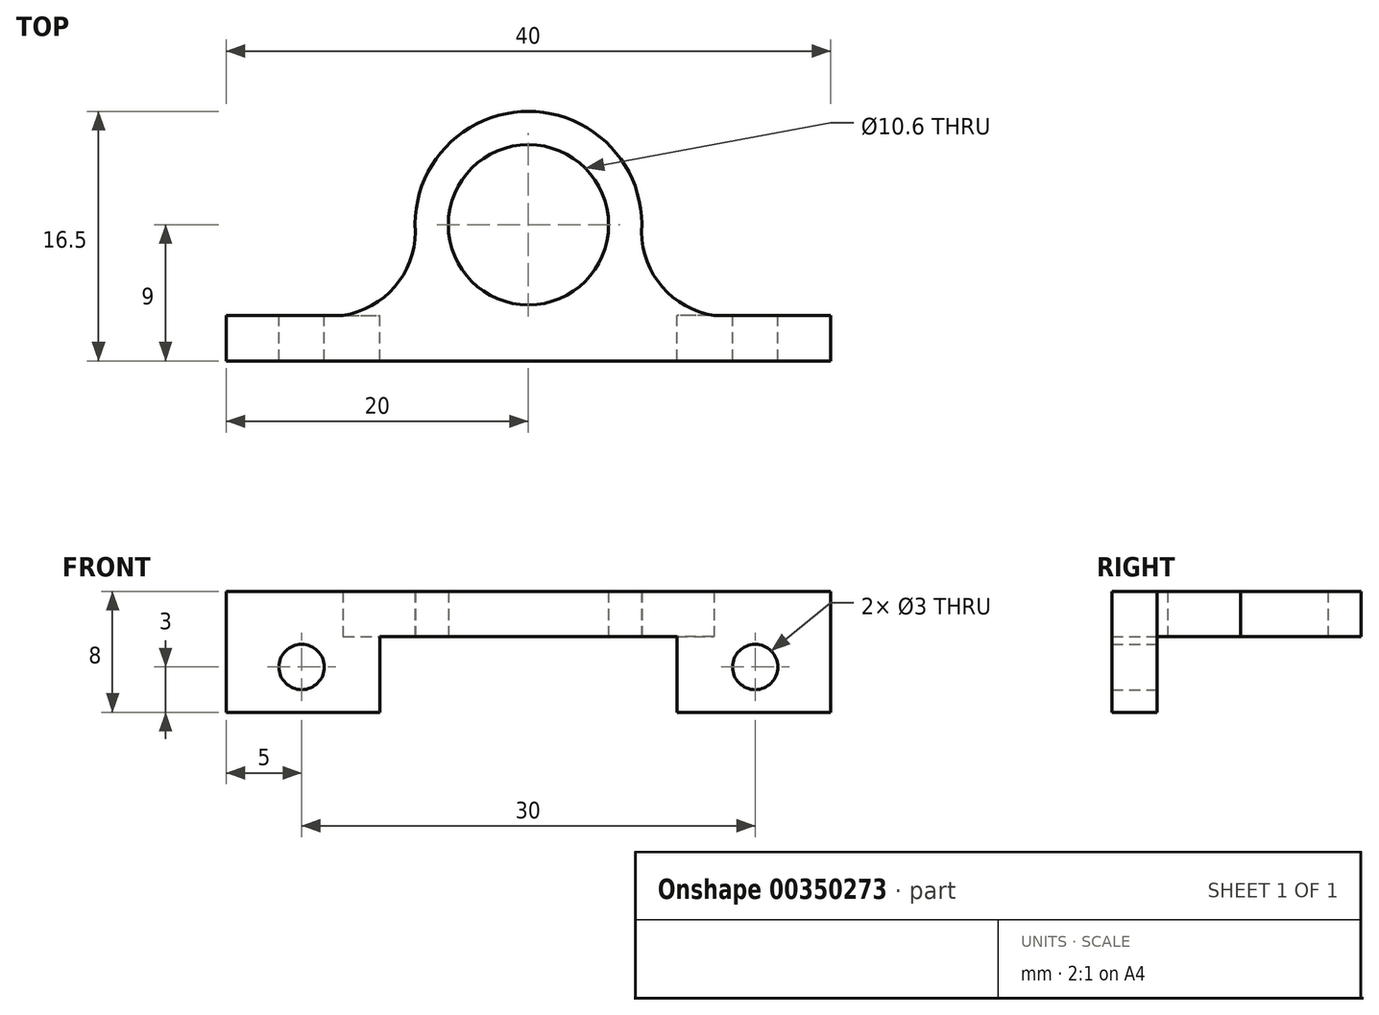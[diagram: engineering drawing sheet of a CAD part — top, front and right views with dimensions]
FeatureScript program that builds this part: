
annotation { "Feature Type Name" : "Feature", "Feature Type Description" : "" }
export const myFeature = defineFeature(function(context is Context, id is Id, definition is map)
    precondition{}
    {
        {
            var Q0;
            Q0=qCreatedBy(makeId("Top.planeOp"),FACE);
            var sketch = newSketch(context, id + "F0", { "sketchPlane" : qUnion([Q0])});
            skLineSegment(sketch, "E0.bottom", {"start": v(-20, 0) * mm, "end": v(-12.26, 0) * mm});
            skLineSegment(sketch, "E0.top", {"start": v(-20, -3) * mm, "end": v(0, -3) * mm});
            skLineSegment(sketch, "E0.left", {"start": v(-20, 0) * mm, "end": v(-20, -3) * mm});
            skCircle(sketch, "E1", {"center": v(0, 6) * mm, "radius": 5.3 * mm});
            skArc(sketch, "E2", {"start": v(7.49, 5.54) * mm, "mid": v(0.22, 13.5) * mm, "end": v(-7.5, 5.97) * mm});
            skArc(sketch, "E3", {"start": v(-12.26, 0) * mm, "mid": v(-8.71, 2.06) * mm, "end": v(-7.5, 5.97) * mm});
            skArc(sketch, "E4.MirrorCS", {"start": v(-7.49, 5.54) * mm, "mid": v(-0.22, 13.5) * mm, "end": v(7.5, 5.97) * mm});
            skArc(sketch, "E5.MirrorCS", {"start": v(12.26, 0) * mm, "mid": v(8.71, 2.06) * mm, "end": v(7.5, 5.97) * mm});
            skLineSegment(sketch, "E6.MirrorCS", {"start": v(20, 0) * mm, "end": v(12.26, 0) * mm});
            skLineSegment(sketch, "E7.MirrorCS", {"start": v(20, 0) * mm, "end": v(20, -3) * mm});
            skLineSegment(sketch, "E8.MirrorCS", {"start": v(20, -3) * mm, "end": v(0, -3) * mm});
            skPoint(sketch, "E9.orphan", {"position": v(0, -1.5) * mm});
            skSolve(sketch);
        }
        {
            var Q0;
            Q0 = qSketchRegion(id + "F0", true);
            extrude(context, id + "F1", {"entities" : qUnion([Q0]), "depth" : 3 * mm});
        }
        {
            var Q0;
            Q0=makeQuery(id+"F1.opExtrude","CAP_FACE",FACE,{"disambiguationData":[OSD([sQuery(id+"F0.wireOp",EDGE,"E0.bottom"),sQuery(id+"F0.wireOp",EDGE,"E0.top"),sQuery(id+"F0.wireOp",EDGE,"E0.left"),sQuery(id+"F0.wireOp",EDGE,"E1"),sQuery(id+"F0.wireOp",EDGE,"E2"),sQuery(id+"F0.wireOp",EDGE,"E3"),sQuery(id+"F0.wireOp",EDGE,"E4.MirrorCS"),sQuery(id+"F0.wireOp",EDGE,"E5.MirrorCS"),sQuery(id+"F0.wireOp",EDGE,"E6.MirrorCS"),sQuery(id+"F0.wireOp",EDGE,"E7.MirrorCS"),sQuery(id+"F0.wireOp",EDGE,"E8.MirrorCS")])],"isStart":true});
            var sketch = newSketch(context, id + "F2", { "sketchPlane" : qUnion([Q0])});
            skLineSegment(sketch, "E10.bottom", {"start": v(-20, 3) * mm, "end": v(-9.82, 3) * mm});
            skLineSegment(sketch, "E10.top", {"start": v(-20, 0) * mm, "end": v(-9.82, 0) * mm});
            skLineSegment(sketch, "E10.left", {"start": v(-20, 3) * mm, "end": v(-20, 0) * mm});
            skLineSegment(sketch, "E10.right", {"start": v(-9.82, 3) * mm, "end": v(-9.82, 0) * mm});
            skLineSegment(sketch, "E11.MirrorCS", {"start": v(9.82, 3) * mm, "end": v(9.82, 0) * mm});
            skLineSegment(sketch, "E12.MirrorCS", {"start": v(20, 3) * mm, "end": v(9.82, 3) * mm});
            skLineSegment(sketch, "E13.MirrorCS", {"start": v(20, 3) * mm, "end": v(20, 0) * mm});
            skLineSegment(sketch, "E14.MirrorCS", {"start": v(20, 0) * mm, "end": v(9.82, 0) * mm});
            skSolve(sketch);
        }
        {
            var Q0;
            Q0 = qSketchRegion(id + "F2", true);
            extrude(context, id + "F3", {"entities" : qUnion([Q0]), "operationType" : NewBodyOperationType.ADD, "depth" : 5 * mm});
        }
        {
            var Q0;
            Q0=makeQuery(id+"F3.boolean.opBoolean","MERGE",FACE,{"derivedFrom":[makeQuery(id+"F1.opExtrude","SWEPT_FACE",FACE,{"disambiguationData":[OSD([sQuery(id+"F0.wireOp",EDGE,"E6.MirrorCS")])]}),makeQuery(id+"F3.opExtrude","SWEPT_FACE",FACE,{"disambiguationData":[OSD([sQuery(id+"F2.wireOp",EDGE,"E14.MirrorCS")])]})]});
            var sketch = newSketch(context, id + "F4", { "sketchPlane" : qUnion([Q0])});
            skCircle(sketch, "E15", {"center": v(-15, -2) * mm, "radius": 1.5 * mm});
            skCircle(sketch, "E16.MirrorC", {"center": v(15, -2) * mm, "radius": 1.5 * mm});
            skSolve(sketch);
        }
        {
            var Q0;
            Q0 = qSketchRegion(id + "F4", true);
            extrude(context, id + "F5", {"entities" : qUnion([Q0]), "operationType" : NewBodyOperationType.REMOVE, "oppositeDirection" : true, "depth" : 5 * mm});
        }
    });
